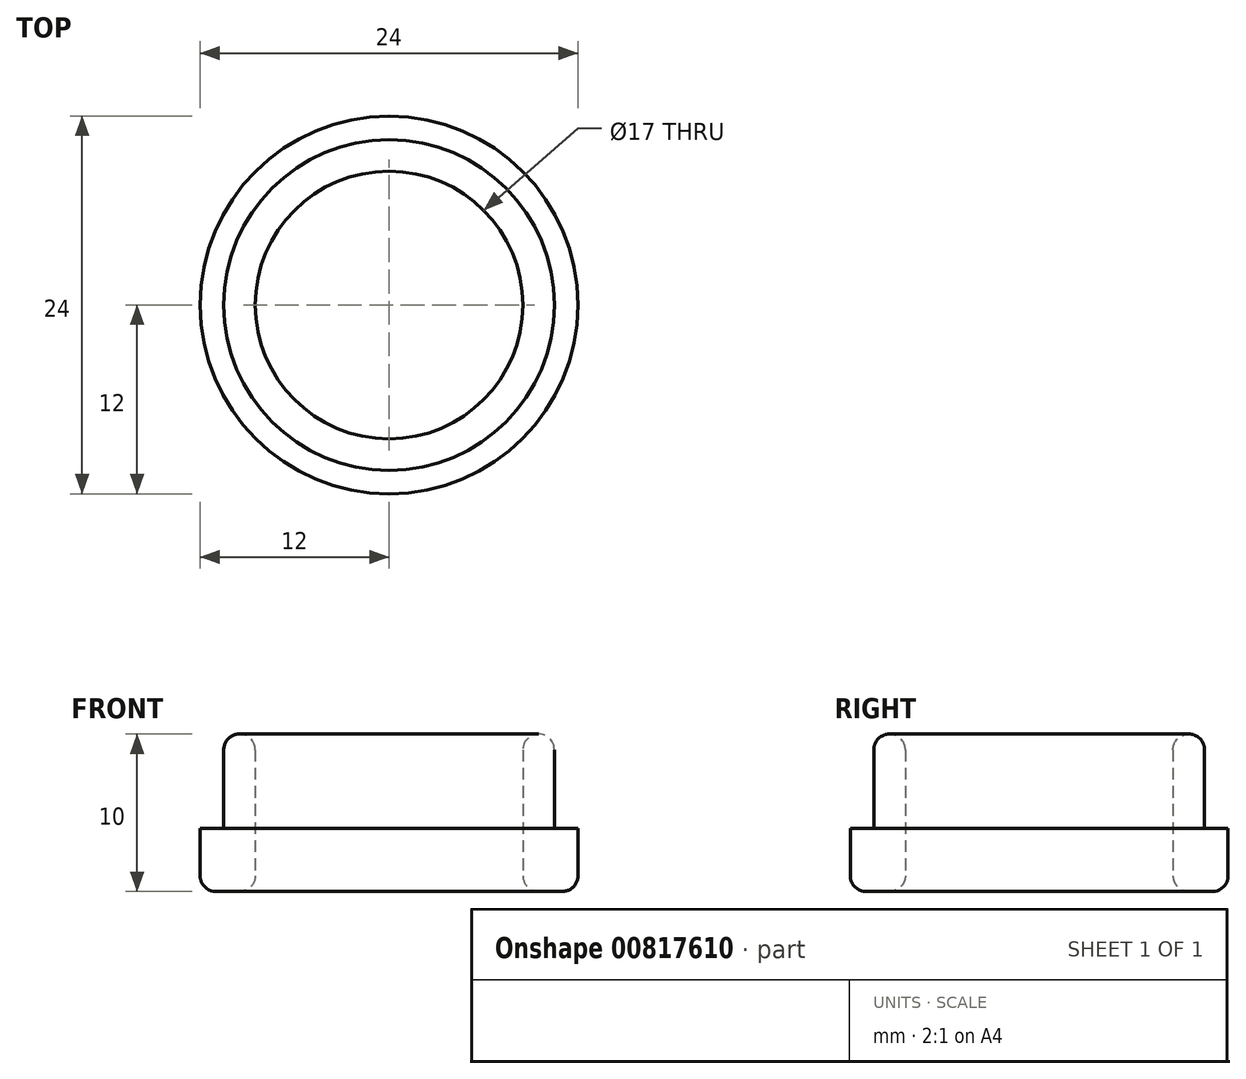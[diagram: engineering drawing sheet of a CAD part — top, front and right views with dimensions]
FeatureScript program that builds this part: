
annotation { "Feature Type Name" : "Feature", "Feature Type Description" : "" }
export const myFeature = defineFeature(function(context is Context, id is Id, definition is map)
    precondition{}
    {
        {
            var Q0;
            Q0=qCreatedBy(makeId("Top.planeOp"),FACE);
            var sketch = newSketch(context, id + "F0", { "sketchPlane" : qUnion([Q0])});
            skCircle(sketch, "E0", {"center": v(0, 0) * mm, "radius": 8.5 * mm});
            skCircle(sketch, "E1", {"center": v(0, 0) * mm, "radius": 10.5 * mm});
            skCircle(sketch, "E2", {"center": v(0, 0) * mm, "radius": 12 * mm});
            skSolve(sketch);
        }
        {
            var Q0;
            Q0=makeQuery(id+"F0.imprint","IMPRINT",FACE,{"disambiguationData":[TD([[makeQuery(id+"F0.imprint","IMPRINT",EDGE,{"derivedFrom":sQuery(id+"F0.wireOp",EDGE,"E0")}),-1.0]])]});
            extrude(context, id + "F1", {"entities" : qUnion([Q0]), "depth" : 10 * mm, "offsetDistance" : 25 * mm});
        }
        {
            var Q0;
            Q0=makeQuery(id+"F0.imprint","IMPRINT",FACE,{"disambiguationData":[TD([[makeQuery(id+"F0.imprint","IMPRINT",EDGE,{"derivedFrom":sQuery(id+"F0.wireOp",EDGE,"E1")}),-1.0]])]});
            extrude(context, id + "F2", {"entities" : qUnion([Q0]), "operationType" : NewBodyOperationType.ADD, "depth" : 4 * mm, "offsetDistance" : 25 * mm});
        }
        {
            var Q0;
            Q0=makeQuery(id+"F1.opExtrude","CAP_EDGE",EDGE,{"disambiguationData":[OSD([sQuery(id+"F0.wireOp",EDGE,"E0")])],"isStart":true});
            var Q1;
            Q1=makeQuery(id+"F2.opExtrude","CAP_EDGE",EDGE,{"disambiguationData":[OSD([sQuery(id+"F0.wireOp",EDGE,"E2")])],"isStart":true});
            var Q2;
            Q2=makeQuery(id+"F1.opExtrude","CAP_EDGE",EDGE,{"disambiguationData":[OSD([sQuery(id+"F0.wireOp",EDGE,"E0")])],"isStart":false});
            var Q3;
            Q3=makeQuery(id+"F1.opExtrude","CAP_EDGE",EDGE,{"disambiguationData":[OSD([sQuery(id+"F0.wireOp",EDGE,"E1")])],"isStart":false});
            fillet(context, id + "F3", {"entities" : qUnion([Q0, Q1, Q2, Q3]), "radius" : 1 * mm, "tangentPropagation" : true, "allowEdgeOverflow" : false});
        }
    });
